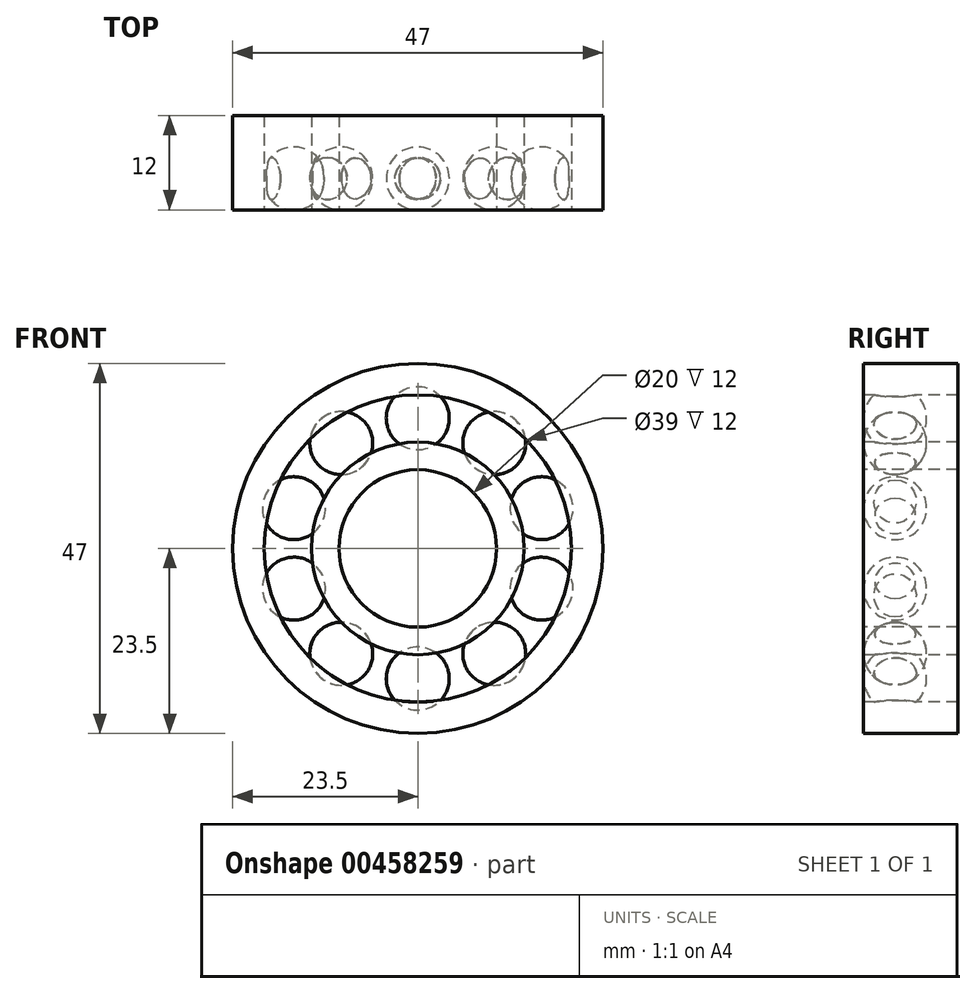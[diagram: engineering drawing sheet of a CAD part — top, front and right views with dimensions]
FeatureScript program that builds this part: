
annotation { "Feature Type Name" : "Feature", "Feature Type Description" : "" }
export const myFeature = defineFeature(function(context is Context, id is Id, definition is map)
    precondition{}
    {
        {
            var Q0;
            Q0=qCreatedBy(makeId("Front.planeOp"),FACE);
            var sketch = newSketch(context, id + "F0", { "sketchPlane" : qUnion([Q0])});
            skCircle(sketch, "E0", {"center": v(0, 0) * mm, "radius": 10 * mm});
            skCircle(sketch, "E1", {"center": v(0, 0) * mm, "radius": 13.5 * mm});
            skCircle(sketch, "E2", {"center": v(0, 0) * mm, "radius": 19.5 * mm});
            skCircle(sketch, "E3", {"center": v(0, 0) * mm, "radius": 23.5 * mm});
            skSolve(sketch);
        }
        {
            var Q0;
            Q0=makeQuery(id+"F0.imprint","IMPRINT",FACE,{"disambiguationData":[TD([[makeQuery(id+"F0.imprint","IMPRINT",EDGE,{"derivedFrom":sQuery(id+"F0.wireOp",EDGE,"E0")}),-1.0]])]});
            var Q1;
            Q1=makeQuery(id+"F0.imprint","IMPRINT",FACE,{"disambiguationData":[TD([[makeQuery(id+"F0.imprint","IMPRINT",EDGE,{"derivedFrom":sQuery(id+"F0.wireOp",EDGE,"E2")}),-1.0]])]});
            extrude(context, id + "F1", {"entities" : qUnion([Q0, Q1]), "oppositeDirection" : true, "depth" : 12 * mm});
        }
        {
            var Q0;
            Q0=qCreatedBy(makeId("Front.planeOp"),FACE);
            cPlane(context, id + "F2", {"entities" : qUnion([Q0]), "cplaneType" : CPlaneType.OFFSET, "offset" : 4 * mm, "oppositeDirection" : true, "width" : 150 * mm, "height" : 150 * mm});
        }
        {
            var Q0;
            Q0=qCreatedBy(id+"F2.planeOp",FACE);
            var sketch = newSketch(context, id + "F3", { "sketchPlane" : qUnion([Q0])});
            skArc(sketch, "E4", {"start": v(0, 20.53) * mm, "mid": v(-4, 16.53) * mm, "end": v(0, 12.53) * mm});
            skLineSegment(sketch, "E5", {"start": v(0, 20.53) * mm, "end": v(0, 12.53) * mm});
            skSolve(sketch);
        }
        {
            var Q0;
            Q0=makeQuery(id+"F3.imprint","IMPRINT",FACE,{"disambiguationData":[TD([[makeQuery(id+"F3.imprint","IMPRINT",EDGE,{"derivedFrom":sQuery(id+"F3.wireOp",EDGE,"E4")}),1.0]])]});
            var Q1;
            Q1=sQuery(id+"F3.wireOp",EDGE,"E5");
            revolve(context, id + "F4", {"entities" : qUnion([Q0]), "axis" : qUnion([Q1]), "revolveType" : RevolveType.FULL});
        }
        {
            var Q0;
            Q0=qCreatedBy(makeId("Right.planeOp"),FACE);
            var sketch = newSketch(context, id + "F5", { "sketchPlane" : qUnion([Q0])});
            skLineSegment(sketch, "E6", {"start": v(0, 0) * mm, "end": v(52.38, 0) * mm, "construction": true});
            skSolve(sketch);
        }
        {
            var Q0;
            Q0=makeQuery(id+"F4.opRevolve","SWEPT_BODY",BODY,{"disambiguationData":[OSD([sQuery(id+"F3.wireOp",EDGE,"E4"),sQuery(id+"F3.wireOp",EDGE,"E5")])]});
            var Q1;
            Q1=sQuery(id+"F5.wireOp",EDGE,"E6");
            circularPattern(context, id + "F6", {"operationType" : NewBodyOperationType.ADD, "entities" : qUnion([Q0]), "axis" : qUnion([Q1]), "angle" : 360 * degree, "instanceCount" : 10, "equalSpace" : true});
        }
    });
